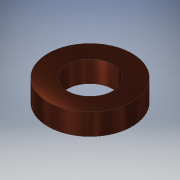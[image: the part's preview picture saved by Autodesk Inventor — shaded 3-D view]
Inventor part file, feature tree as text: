
AUTODESK INVENTOR PART (.ipt)
format: ipt  version: 2019 (Build 230136000, 136)  size: 104,448 bytes
history: native  units: mm
features: extrude x1, sketch x1
ambient origin geometry x8: Origin, YZ Plane, XZ Plane, XY Plane, X Axis, Y Axis, Z Axis, Center Point
bodies: Solid1 (feature_tree)
feature tree (2):
  extrude  "Extrusion1"  Depth=700.0mm
  sketch  "Sketch1"  dims[d0=1500.0mm d1=2750.0mm d2=700.0mm d3=0.0mm]
